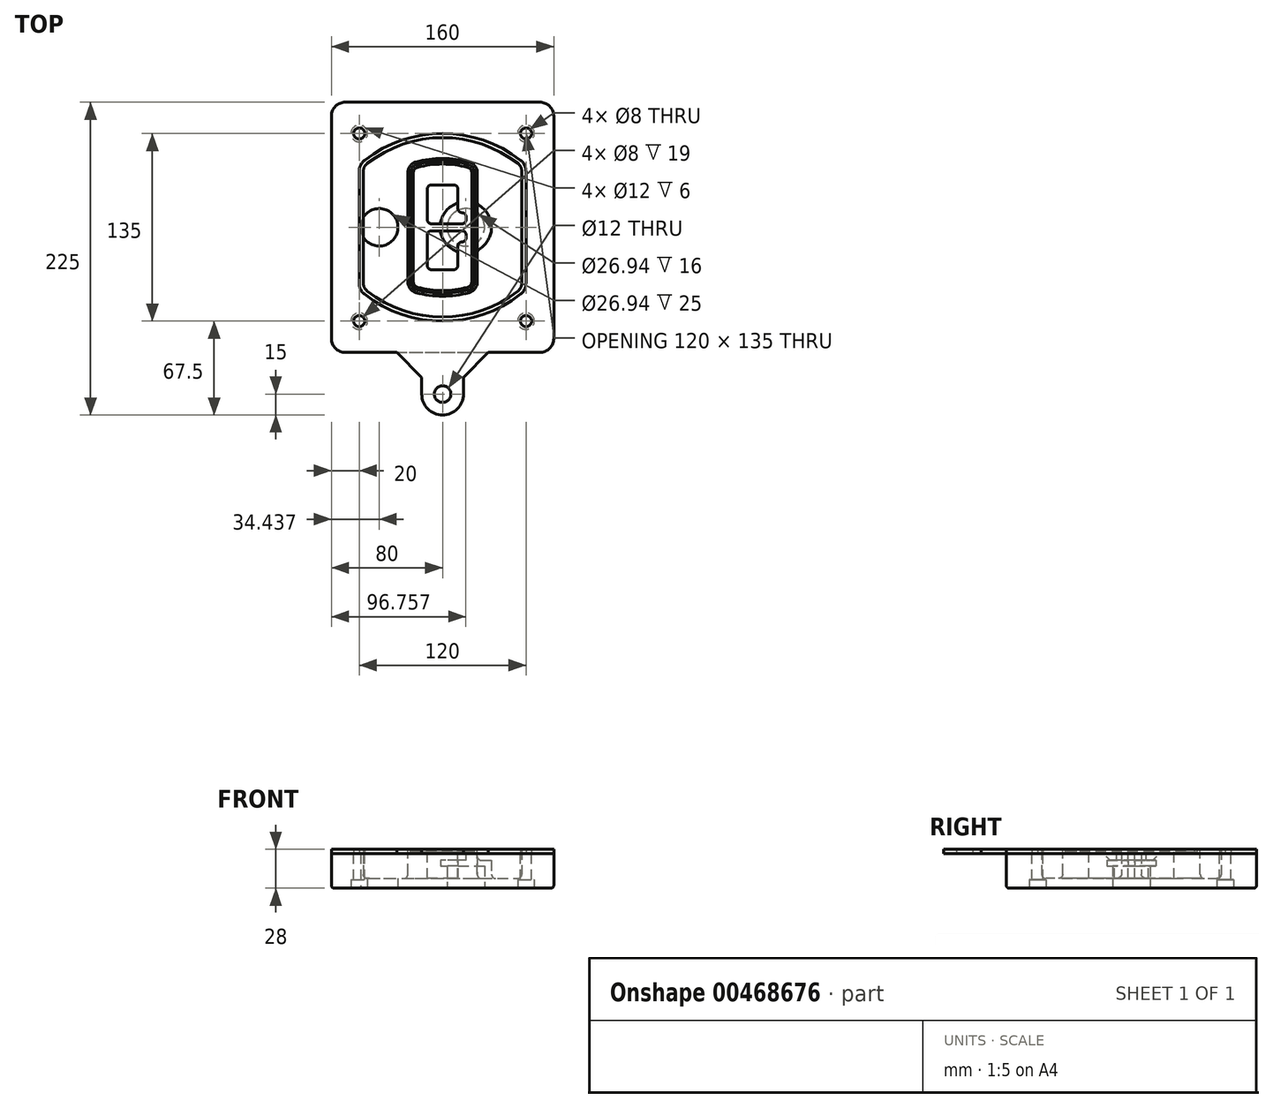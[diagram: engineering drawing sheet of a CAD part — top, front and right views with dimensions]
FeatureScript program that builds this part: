
annotation { "Feature Type Name" : "Feature", "Feature Type Description" : "" }
export const myFeature = defineFeature(function(context is Context, id is Id, definition is map)
    precondition{}
    {
        {
            var Q0;
            Q0=qCreatedBy(makeId("Top.planeOp"),FACE);
            var sketch = newSketch(context, id + "F0", { "sketchPlane" : qUnion([Q0])});
            skPoint(sketch, "E0.rect.middle", {"position": v(0, 0) * mm});
            skLineSegment(sketch, "E1.bottom", {"start": v(-70, -90) * mm, "end": v(70, -90) * mm});
            skLineSegment(sketch, "E1.top", {"start": v(-70, 90) * mm, "end": v(70, 90) * mm});
            skLineSegment(sketch, "E1.left", {"start": v(-80, -80) * mm, "end": v(-80, 80) * mm});
            skLineSegment(sketch, "E1.right", {"start": v(80, -80) * mm, "end": v(80, 80) * mm});
            skLineSegment(sketch, "E2", {"start": v(-80, 90) * mm, "end": v(80, -90) * mm, "construction": true});
            skLineSegment(sketch, "E3", {"start": v(80, 90) * mm, "end": v(-80, -90) * mm, "construction": true});
            skCircle(sketch, "E4", {"center": v(-60, 67.5) * mm, "radius": 4 * mm});
            skCircle(sketch, "E5", {"center": v(60, 67.5) * mm, "radius": 4 * mm});
            skCircle(sketch, "E6", {"center": v(60, -67.5) * mm, "radius": 4 * mm});
            skCircle(sketch, "E7", {"center": v(-60, -67.5) * mm, "radius": 4 * mm});
            skLineSegment(sketch, "E8", {"start": v(-60, 67.5) * mm, "end": v(60, 67.5) * mm, "construction": true});
            skLineSegment(sketch, "E9", {"start": v(60, 67.5) * mm, "end": v(60, -67.5) * mm, "construction": true});
            skLineSegment(sketch, "E10", {"start": v(60, -67.5) * mm, "end": v(-60, -67.5) * mm, "construction": true});
            skLineSegment(sketch, "E11", {"start": v(-60, -67.5) * mm, "end": v(-60, 67.5) * mm, "construction": true});
            skLineSegment(sketch, "E12", {"start": v(-60, 40.3) * mm, "end": v(-60, -40.3) * mm});
            skLineSegment(sketch, "E13", {"start": v(60, 40.3) * mm, "end": v(60, -40.3) * mm});
            skArc(sketch, "E14", {"start": v(56.15, 48.18) * mm, "mid": v(0, 67.5) * mm, "end": v(-56.15, 48.18) * mm});
            skArc(sketch, "E15", {"start": v(-56.15, -48.18) * mm, "mid": v(0, -67.5) * mm, "end": v(56.15, -48.18) * mm});
            skLineSegment(sketch, "E16", {"start": v(-60, 0) * mm, "end": v(60, 0) * mm, "construction": true});
            skPoint(sketch, "E17.visualSharp", {"position": v(-60, -45) * mm});
            skArc(sketch, "E17.filletArc", {"start": v(-60, -40.3) * mm, "mid": v(-58.99, -44.68) * mm, "end": v(-56.15, -48.18) * mm});
            skPoint(sketch, "E18.visualSharp", {"position": v(-60, 45) * mm});
            skArc(sketch, "E18.filletArc", {"start": v(-56.15, 48.18) * mm, "mid": v(-58.99, 44.68) * mm, "end": v(-60, 40.3) * mm});
            skPoint(sketch, "E19.visualSharp", {"position": v(60, 45) * mm});
            skArc(sketch, "E19.filletArc", {"start": v(60, 40.3) * mm, "mid": v(58.99, 44.68) * mm, "end": v(56.15, 48.18) * mm});
            skPoint(sketch, "E20.visualSharp", {"position": v(60, -45) * mm});
            skArc(sketch, "E20.filletArc", {"start": v(56.15, -48.18) * mm, "mid": v(58.99, -44.68) * mm, "end": v(60, -40.3) * mm});
            skPoint(sketch, "E21.visualSharp", {"position": v(-80, 90) * mm});
            skArc(sketch, "E21.filletArc", {"start": v(-70, 90) * mm, "mid": v(-77.07, 87.07) * mm, "end": v(-80, 80) * mm});
            skPoint(sketch, "E22.visualSharp", {"position": v(80, 90) * mm});
            skArc(sketch, "E22.filletArc", {"start": v(80, 80) * mm, "mid": v(77.07, 87.07) * mm, "end": v(70, 90) * mm});
            skPoint(sketch, "E23.visualSharp", {"position": v(80, -90) * mm});
            skArc(sketch, "E23.filletArc", {"start": v(70, -90) * mm, "mid": v(77.07, -87.07) * mm, "end": v(80, -80) * mm});
            skPoint(sketch, "E24.visualSharp", {"position": v(-80, -90) * mm});
            skArc(sketch, "E24.filletArc", {"start": v(-80, -80) * mm, "mid": v(-77.07, -87.07) * mm, "end": v(-70, -90) * mm});
            skArc(sketch, "E25.0", {"start": v(57, 40.3) * mm, "mid": v(56.3, 43.36) * mm, "end": v(54.3, 45.81) * mm});
            skLineSegment(sketch, "E25.1", {"start": v(57, 40.3) * mm, "end": v(57, -40.3) * mm});
            skArc(sketch, "E25.2", {"start": v(54.3, -45.81) * mm, "mid": v(56.3, -43.36) * mm, "end": v(57, -40.3) * mm});
            skArc(sketch, "E25.3", {"start": v(-54.3, -45.81) * mm, "mid": v(0, -64.5) * mm, "end": v(54.3, -45.81) * mm});
            skArc(sketch, "E25.4", {"start": v(-57, -40.3) * mm, "mid": v(-56.3, -43.36) * mm, "end": v(-54.3, -45.81) * mm});
            skArc(sketch, "E25.5", {"start": v(54.3, 45.81) * mm, "mid": v(0, 64.5) * mm, "end": v(-54.3, 45.81) * mm});
            skLineSegment(sketch, "E25.6", {"start": v(-57, 40.3) * mm, "end": v(-57, -40.3) * mm});
            skArc(sketch, "E25.7", {"start": v(-54.3, 45.81) * mm, "mid": v(-56.3, 43.36) * mm, "end": v(-57, 40.3) * mm});
            skArc(sketch, "E26.0", {"start": v(-58.62, 51.33) * mm, "mid": v(-62.58, 46.43) * mm, "end": v(-64, 40.3) * mm});
            skArc(sketch, "E26.1", {"start": v(58.62, 51.33) * mm, "mid": v(0, 71.5) * mm, "end": v(-58.62, 51.33) * mm});
            skArc(sketch, "E26.2", {"start": v(64, 40.3) * mm, "mid": v(62.58, 46.43) * mm, "end": v(58.62, 51.33) * mm});
            skLineSegment(sketch, "E26.3", {"start": v(64, 40.3) * mm, "end": v(64, -40.3) * mm});
            skArc(sketch, "E26.4", {"start": v(58.62, -51.33) * mm, "mid": v(62.58, -46.43) * mm, "end": v(64, -40.3) * mm});
            skLineSegment(sketch, "E26.5", {"start": v(-64, 40.3) * mm, "end": v(-64, -40.3) * mm});
            skArc(sketch, "E26.6", {"start": v(-58.62, -51.33) * mm, "mid": v(0, -71.5) * mm, "end": v(58.62, -51.33) * mm});
            skArc(sketch, "E26.7", {"start": v(-64, -40.3) * mm, "mid": v(-62.58, -46.43) * mm, "end": v(-58.62, -51.33) * mm});
            skSolve(sketch);
        }
        {
            var Q0;
            Q0=makeQuery(id+"F0.imprint","IMPRINT",FACE,{"disambiguationData":[TD([[makeQuery(id+"F0.imprint","IMPRINT",EDGE,{"derivedFrom":sQuery(id+"F0.wireOp",EDGE,"E1.bottom")}),1.0]])]});
            var Q1;
            Q1=makeQuery(id+"F0.imprint","IMPRINT",FACE,{"disambiguationData":[TD([[makeQuery(id+"F0.imprint","IMPRINT",EDGE,{"derivedFrom":sQuery(id+"F0.wireOp",EDGE,"E12")}),1.0]])]});
            var Q2;
            Q2=makeQuery(id+"F0.imprint","IMPRINT",FACE,{"disambiguationData":[TD([[makeQuery(id+"F0.imprint","IMPRINT",EDGE,{"derivedFrom":sQuery(id+"F0.wireOp",EDGE,"E25.0")}),1.0]])]});
            var Q3;
            Q3=makeQuery(id+"F0.imprint","IMPRINT",FACE,{"disambiguationData":[TD([[makeQuery(id+"F0.imprint","IMPRINT",EDGE,{"derivedFrom":sQuery(id+"F0.wireOp",EDGE,"E12")}),-1.0]])]});
            extrude(context, id + "F1", {"entities" : qUnion([Q0, Q1, Q2, Q3]), "oppositeDirection" : true, "depth" : 25 * mm});
        }
        {
            var Q0;
            Q0=makeQuery(id+"F0.imprint","IMPRINT",FACE,{"disambiguationData":[TD([[makeQuery(id+"F0.imprint","IMPRINT",EDGE,{"derivedFrom":sQuery(id+"F0.wireOp",EDGE,"E12")}),1.0]])]});
            extrude(context, id + "F2", {"entities" : qUnion([Q0]), "operationType" : NewBodyOperationType.ADD, "depth" : 3 * mm});
        }
        {
            var Q0;
            Q0=makeQuery(id+"F0.imprint","IMPRINT",FACE,{"disambiguationData":[TD([[makeQuery(id+"F0.imprint","IMPRINT",EDGE,{"derivedFrom":sQuery(id+"F0.wireOp",EDGE,"E25.0")}),1.0]])]});
            extrude(context, id + "F3", {"entities" : qUnion([Q0]), "operationType" : NewBodyOperationType.REMOVE, "oppositeDirection" : true, "depth" : 18 * mm});
        }
        {
            var Q0;
            Q0=makeQuery(id+"F2.opExtrude","CAP_FACE",FACE,{"disambiguationData":[OSD([sQuery(id+"F0.wireOp",EDGE,"E12"),sQuery(id+"F0.wireOp",EDGE,"E13"),sQuery(id+"F0.wireOp",EDGE,"E14"),sQuery(id+"F0.wireOp",EDGE,"E15"),sQuery(id+"F0.wireOp",EDGE,"E17.filletArc"),sQuery(id+"F0.wireOp",EDGE,"E18.filletArc"),sQuery(id+"F0.wireOp",EDGE,"E19.filletArc"),sQuery(id+"F0.wireOp",EDGE,"E20.filletArc"),sQuery(id+"F0.wireOp",EDGE,"E25.0"),sQuery(id+"F0.wireOp",EDGE,"E25.1"),sQuery(id+"F0.wireOp",EDGE,"E25.2"),sQuery(id+"F0.wireOp",EDGE,"E25.3"),sQuery(id+"F0.wireOp",EDGE,"E25.4"),sQuery(id+"F0.wireOp",EDGE,"E25.5"),sQuery(id+"F0.wireOp",EDGE,"E25.6"),sQuery(id+"F0.wireOp",EDGE,"E25.7")])],"isStart":false});
            var sketch = newSketch(context, id + "F4", { "sketchPlane" : qUnion([Q0])});
            skArc(sketch, "E27.0", {"start": v(-19.08, -46.97) * mm, "mid": v(0, -49.5) * mm, "end": v(19.08, -46.97) * mm});
            skArc(sketch, "E28.0", {"start": v(19.08, 46.97) * mm, "mid": v(0, 49.5) * mm, "end": v(-19.08, 46.97) * mm});
            skLineSegment(sketch, "E29", {"start": v(-25, 39.25) * mm, "end": v(-25, -39.25) * mm});
            skLineSegment(sketch, "E30", {"start": v(25, 39.25) * mm, "end": v(25, -39.25) * mm});
            skLineSegment(sketch, "E31", {"start": v(-25, 45.1) * mm, "end": v(25, 45.1) * mm, "construction": true});
            skLineSegment(sketch, "E32", {"start": v(-25, -45.1) * mm, "end": v(25, -45.1) * mm, "construction": true});
            skPoint(sketch, "E33.visualSharp", {"position": v(-25, 45.1) * mm});
            skArc(sketch, "E33.filletArc", {"start": v(-19.08, 46.97) * mm, "mid": v(-23.35, 44.11) * mm, "end": v(-25, 39.25) * mm});
            skPoint(sketch, "E34.visualSharp", {"position": v(25, 45.1) * mm});
            skArc(sketch, "E34.filletArc", {"start": v(25, 39.25) * mm, "mid": v(23.35, 44.11) * mm, "end": v(19.08, 46.97) * mm});
            skPoint(sketch, "E35.visualSharp", {"position": v(25, -45.1) * mm});
            skArc(sketch, "E35.filletArc", {"start": v(19.08, -46.97) * mm, "mid": v(23.35, -44.11) * mm, "end": v(25, -39.25) * mm});
            skPoint(sketch, "E36.visualSharp", {"position": v(-25, -45.1) * mm});
            skArc(sketch, "E36.filletArc", {"start": v(-25, -39.25) * mm, "mid": v(-23.35, -44.11) * mm, "end": v(-19.08, -46.97) * mm});
            skArc(sketch, "E37.0", {"start": v(54.3, 45.81) * mm, "mid": v(0, 64.5) * mm, "end": v(-54.3, 45.81) * mm});
            skArc(sketch, "E37.1", {"start": v(-54.3, 45.81) * mm, "mid": v(-56.3, 43.36) * mm, "end": v(-57, 40.3) * mm});
            skLineSegment(sketch, "E37.2", {"start": v(-57, 40.3) * mm, "end": v(-57, -40.3) * mm});
            skArc(sketch, "E37.3", {"start": v(-57, -40.3) * mm, "mid": v(-56.3, -43.36) * mm, "end": v(-54.3, -45.81) * mm});
            skArc(sketch, "E37.4", {"start": v(-54.3, -45.81) * mm, "mid": v(0, -64.5) * mm, "end": v(54.3, -45.81) * mm});
            skArc(sketch, "E37.5", {"start": v(54.3, -45.81) * mm, "mid": v(56.3, -43.36) * mm, "end": v(57, -40.3) * mm});
            skLineSegment(sketch, "E37.6", {"start": v(57, 40.3) * mm, "end": v(57, -40.3) * mm});
            skArc(sketch, "E37.7", {"start": v(57, 40.3) * mm, "mid": v(56.3, 43.36) * mm, "end": v(54.3, 45.81) * mm});
            skLineSegment(sketch, "E38.0", {"start": v(23, 39.25) * mm, "end": v(23, -39.25) * mm});
            skArc(sketch, "E38.1", {"start": v(18.56, -45.04) * mm, "mid": v(21.76, -42.9) * mm, "end": v(23, -39.25) * mm});
            skArc(sketch, "E38.2", {"start": v(-18.56, -45.04) * mm, "mid": v(0, -47.5) * mm, "end": v(18.56, -45.04) * mm});
            skArc(sketch, "E38.3", {"start": v(-23, -39.25) * mm, "mid": v(-21.76, -42.9) * mm, "end": v(-18.56, -45.04) * mm});
            skLineSegment(sketch, "E38.4", {"start": v(-23, 39.25) * mm, "end": v(-23, -39.25) * mm});
            skArc(sketch, "E38.5", {"start": v(23, 39.25) * mm, "mid": v(21.76, 42.9) * mm, "end": v(18.56, 45.04) * mm});
            skArc(sketch, "E38.6", {"start": v(-18.56, 45.04) * mm, "mid": v(-21.76, 42.9) * mm, "end": v(-23, 39.25) * mm});
            skArc(sketch, "E38.7", {"start": v(18.56, 45.04) * mm, "mid": v(0, 47.5) * mm, "end": v(-18.56, 45.04) * mm});
            skArc(sketch, "E39.0", {"start": v(21, 39.25) * mm, "mid": v(20.18, 41.68) * mm, "end": v(18.04, 43.1) * mm});
            skLineSegment(sketch, "E39.1", {"start": v(21, 39.25) * mm, "end": v(21, -39.25) * mm});
            skArc(sketch, "E39.2", {"start": v(18.04, -43.1) * mm, "mid": v(20.18, -41.68) * mm, "end": v(21, -39.25) * mm});
            skArc(sketch, "E39.3", {"start": v(-18.04, -43.1) * mm, "mid": v(0, -45.5) * mm, "end": v(18.04, -43.1) * mm});
            skArc(sketch, "E39.4", {"start": v(-21, -39.25) * mm, "mid": v(-20.18, -41.68) * mm, "end": v(-18.04, -43.1) * mm});
            skArc(sketch, "E39.5", {"start": v(18.04, 43.1) * mm, "mid": v(0, 45.5) * mm, "end": v(-18.04, 43.1) * mm});
            skLineSegment(sketch, "E39.6", {"start": v(-21, 39.25) * mm, "end": v(-21, -39.25) * mm});
            skArc(sketch, "E39.7", {"start": v(-18.04, 43.1) * mm, "mid": v(-20.18, 41.68) * mm, "end": v(-21, 39.25) * mm});
            skLineSegment(sketch, "E40", {"start": v(-25, 0) * mm, "end": v(25, 0) * mm, "construction": true});
            skLineSegment(sketch, "E41", {"start": v(-11, 5.5) * mm, "end": v(-11, 27.5) * mm});
            skLineSegment(sketch, "E42", {"start": v(-8, 30.5) * mm, "end": v(8, 30.5) * mm});
            skLineSegment(sketch, "E43", {"start": v(11, 27.5) * mm, "end": v(11, 13.5) * mm});
            skLineSegment(sketch, "E44", {"start": v(14, 10.5) * mm, "end": v(14, 10.5) * mm});
            skLineSegment(sketch, "E45", {"start": v(17, 7.5) * mm, "end": v(17, 5.5) * mm});
            skLineSegment(sketch, "E46", {"start": v(14, 2.5) * mm, "end": v(-8, 2.5) * mm});
            skPoint(sketch, "E47.visualSharp", {"position": v(-11, 30.5) * mm});
            skArc(sketch, "E47.filletArc", {"start": v(-8, 30.5) * mm, "mid": v(-10.12, 29.62) * mm, "end": v(-11, 27.5) * mm});
            skPoint(sketch, "E48.visualSharp", {"position": v(11, 30.5) * mm});
            skArc(sketch, "E48.filletArc", {"start": v(11, 27.5) * mm, "mid": v(10.12, 29.62) * mm, "end": v(8, 30.5) * mm});
            skPoint(sketch, "E49.visualSharp", {"position": v(11, 10.5) * mm});
            skArc(sketch, "E49.filletArc", {"start": v(11, 13.5) * mm, "mid": v(11.88, 11.38) * mm, "end": v(14, 10.5) * mm});
            skPoint(sketch, "E50.visualSharp", {"position": v(17, 10.5) * mm});
            skArc(sketch, "E50.filletArc", {"start": v(17, 7.5) * mm, "mid": v(16.12, 9.62) * mm, "end": v(14, 10.5) * mm});
            skPoint(sketch, "E51.visualSharp", {"position": v(17, 2.5) * mm});
            skArc(sketch, "E51.filletArc", {"start": v(14, 2.5) * mm, "mid": v(16.12, 3.38) * mm, "end": v(17, 5.5) * mm});
            skPoint(sketch, "E52.visualSharp", {"position": v(-11, 2.5) * mm});
            skArc(sketch, "E52.filletArc", {"start": v(-11, 5.5) * mm, "mid": v(-10.12, 3.38) * mm, "end": v(-8, 2.5) * mm});
            skLineSegment(sketch, "E53.0.MirrorCS", {"start": v(14, -2.5) * mm, "end": v(-8, -2.5) * mm});
            skArc(sketch, "E54.0.MirrorCS", {"start": v(-11, -5.5) * mm, "mid": v(-10.12, -3.38) * mm, "end": v(-8, -2.5) * mm});
            skLineSegment(sketch, "E55.0.MirrorCS", {"start": v(-11, -5.5) * mm, "end": v(-11, -27.5) * mm});
            skArc(sketch, "E56.0.MirrorCS", {"start": v(-8, -30.5) * mm, "mid": v(-10.12, -29.62) * mm, "end": v(-11, -27.5) * mm});
            skLineSegment(sketch, "E57.0.MirrorCS", {"start": v(-8, -30.5) * mm, "end": v(8, -30.5) * mm});
            skArc(sketch, "E58.0.MirrorCS", {"start": v(11, -27.5) * mm, "mid": v(10.12, -29.62) * mm, "end": v(8, -30.5) * mm});
            skLineSegment(sketch, "E59.0.MirrorCS", {"start": v(11, -27.5) * mm, "end": v(11, -13.5) * mm});
            skArc(sketch, "E60.0.MirrorCS", {"start": v(11, -13.5) * mm, "mid": v(11.88, -11.38) * mm, "end": v(14, -10.5) * mm});
            skArc(sketch, "E61.0.MirrorCS", {"start": v(17, -7.5) * mm, "mid": v(16.12, -9.62) * mm, "end": v(14, -10.5) * mm});
            skLineSegment(sketch, "E62.0.MirrorCS", {"start": v(17, -7.5) * mm, "end": v(17, -5.5) * mm});
            skArc(sketch, "E63.0.MirrorCS", {"start": v(14, -2.5) * mm, "mid": v(16.12, -3.38) * mm, "end": v(17, -5.5) * mm});
            skSolve(sketch);
        }
        {
            var Q0;
            Q0=makeQuery(id+"F4.imprint","IMPRINT",FACE,{"disambiguationData":[TD([[makeQuery(id+"F4.imprint","IMPRINT",EDGE,{"derivedFrom":sQuery(id+"F4.wireOp",EDGE,"E27.0")}),1.0]])]});
            var Q1;
            Q1=makeQuery(id+"F4.imprint","IMPRINT",FACE,{"disambiguationData":[TD([[makeQuery(id+"F4.imprint","IMPRINT",EDGE,{"derivedFrom":sQuery(id+"F4.wireOp",EDGE,"E38.0")}),-1.0]])]});
            var Q2;
            Q2=makeQuery(id+"F4.imprint","IMPRINT",FACE,{"disambiguationData":[TD([[makeQuery(id+"F4.imprint","IMPRINT",EDGE,{"derivedFrom":sQuery(id+"F4.wireOp",EDGE,"E39.0")}),1.0]])]});
            extrude(context, id + "F5", {"entities" : qUnion([Q0, Q1, Q2]), "operationType" : NewBodyOperationType.ADD, "endBound" : BoundingType.UP_TO_NEXT, "oppositeDirection" : true, "depth" : 25 * mm});
        }
        {
            var Q0;
            Q0=makeQuery(id+"F4.imprint","IMPRINT",FACE,{"disambiguationData":[TD([[makeQuery(id+"F4.imprint","IMPRINT",EDGE,{"derivedFrom":sQuery(id+"F4.wireOp",EDGE,"E38.0")}),-1.0]])]});
            extrude(context, id + "F6", {"entities" : qUnion([Q0]), "operationType" : NewBodyOperationType.REMOVE, "oppositeDirection" : true, "depth" : 2 * mm});
        }
        {
            var Q0;
            Q0=makeQuery(id+"F1.opExtrude","CAP_FACE",FACE,{"disambiguationData":[OSD([sQuery(id+"F0.wireOp",EDGE,"E1.bottom"),sQuery(id+"F0.wireOp",EDGE,"E1.top"),sQuery(id+"F0.wireOp",EDGE,"E1.left"),sQuery(id+"F0.wireOp",EDGE,"E1.right"),sQuery(id+"F0.wireOp",EDGE,"E4"),sQuery(id+"F0.wireOp",EDGE,"E5"),sQuery(id+"F0.wireOp",EDGE,"E6"),sQuery(id+"F0.wireOp",EDGE,"E7"),sQuery(id+"F0.wireOp",EDGE,"E21.filletArc"),sQuery(id+"F0.wireOp",EDGE,"E22.filletArc"),sQuery(id+"F0.wireOp",EDGE,"E23.filletArc"),sQuery(id+"F0.wireOp",EDGE,"E24.filletArc")])],"isStart":false});
            var sketch = newSketch(context, id + "F7", { "sketchPlane" : qUnion([Q0])});
            skCircle(sketch, "E64", {"center": v(16.76, 0) * mm, "radius": 13.47 * mm});
            skCircle(sketch, "E65", {"center": v(-45.56, 0) * mm, "radius": 13.47 * mm});
            skLineSegment(sketch, "E66", {"start": v(80, 0) * mm, "end": v(-80, 0) * mm});
            skCircle(sketch, "E67", {"center": v(16.76, 0) * mm, "radius": 18.47 * mm});
            skCircle(sketch, "E68", {"center": v(60, -67.5) * mm, "radius": 6 * mm});
            skCircle(sketch, "E69", {"center": v(-60, -67.5) * mm, "radius": 6 * mm});
            skCircle(sketch, "E70", {"center": v(-60, 67.5) * mm, "radius": 6 * mm});
            skCircle(sketch, "E71", {"center": v(60, 67.5) * mm, "radius": 6 * mm});
            skSolve(sketch);
        }
        {
            var Q0;
            {var subQ1=sQuery(id+"F7.wireOp",EDGE,"E66");var subQ4=sQuery(id+"F7.wireOp",EDGE,"E64");var subQ6=makeQuery(id+"F7.imprint","INTERSECT",VERTEX,{"disambiguationData":[OD(0.0)],"derivedFrom":[subQ4,subQ1]});Q0=makeQuery(id+"F7.imprint","IMPRINT",FACE,{"disambiguationData":[TD([[makeQuery(id+"F7.imprint","IMPRINT",EDGE,{"disambiguationData":[TD([[subQ6,-1.0]])],"derivedFrom":subQ4}),-1.0]])]});}
            var Q1;
            {var subQ0=sQuery(id+"F7.wireOp",EDGE,"E66");var subQ1=sQuery(id+"F7.wireOp",EDGE,"E64");var subQ3=makeQuery(id+"F7.imprint","INTERSECT",VERTEX,{"disambiguationData":[OD(0.0)],"derivedFrom":[subQ1,subQ0]});Q1=makeQuery(id+"F7.imprint","IMPRINT",FACE,{"disambiguationData":[TD([[makeQuery(id+"F7.imprint","IMPRINT",EDGE,{"disambiguationData":[TD([[subQ3,-1.0]])],"derivedFrom":subQ1}),1.0]])]});}
            var Q2;
            {var subQ0=sQuery(id+"F7.wireOp",EDGE,"E66");var subQ1=sQuery(id+"F7.wireOp",EDGE,"E64");var subQ3=makeQuery(id+"F7.imprint","INTERSECT",VERTEX,{"disambiguationData":[OD(0.0)],"derivedFrom":[subQ1,subQ0]});Q2=makeQuery(id+"F7.imprint","IMPRINT",FACE,{"disambiguationData":[TD([[makeQuery(id+"F7.imprint","IMPRINT",EDGE,{"disambiguationData":[TD([[subQ3,1.0]])],"derivedFrom":subQ1}),1.0]])]});}
            var Q3;
            {var subQ1=sQuery(id+"F7.wireOp",EDGE,"E66");var subQ4=sQuery(id+"F7.wireOp",EDGE,"E64");var subQ6=makeQuery(id+"F7.imprint","INTERSECT",VERTEX,{"disambiguationData":[OD(0.0)],"derivedFrom":[subQ4,subQ1]});Q3=makeQuery(id+"F7.imprint","IMPRINT",FACE,{"disambiguationData":[TD([[makeQuery(id+"F7.imprint","IMPRINT",EDGE,{"disambiguationData":[TD([[subQ6,1.0]])],"derivedFrom":subQ4}),-1.0]])]});}
            extrude(context, id + "F8", {"entities" : qUnion([Q0, Q1, Q2, Q3]), "operationType" : NewBodyOperationType.ADD, "oppositeDirection" : true, "depth" : 20 * mm});
        }
        {
            var Q0;
            {var subQ0=sQuery(id+"F7.wireOp",EDGE,"E66");var subQ1=sQuery(id+"F7.wireOp",EDGE,"E64");var subQ3=makeQuery(id+"F7.imprint","INTERSECT",VERTEX,{"disambiguationData":[OD(0.0)],"derivedFrom":[subQ1,subQ0]});Q0=makeQuery(id+"F7.imprint","IMPRINT",FACE,{"disambiguationData":[TD([[makeQuery(id+"F7.imprint","IMPRINT",EDGE,{"disambiguationData":[TD([[subQ3,-1.0]])],"derivedFrom":subQ1}),1.0]])]});}
            var Q1;
            {var subQ0=sQuery(id+"F7.wireOp",EDGE,"E66");var subQ1=sQuery(id+"F7.wireOp",EDGE,"E64");var subQ3=makeQuery(id+"F7.imprint","INTERSECT",VERTEX,{"disambiguationData":[OD(0.0)],"derivedFrom":[subQ1,subQ0]});Q1=makeQuery(id+"F7.imprint","IMPRINT",FACE,{"disambiguationData":[TD([[makeQuery(id+"F7.imprint","IMPRINT",EDGE,{"disambiguationData":[TD([[subQ3,1.0]])],"derivedFrom":subQ1}),1.0]])]});}
            extrude(context, id + "F9", {"entities" : qUnion([Q0, Q1]), "operationType" : NewBodyOperationType.REMOVE, "oppositeDirection" : true, "depth" : 16 * mm});
        }
        {
            var Q0;
            {var subQ0=sQuery(id+"F7.wireOp",EDGE,"E66");var subQ1=sQuery(id+"F7.wireOp",EDGE,"E65");var subQ3=makeQuery(id+"F7.imprint","INTERSECT",VERTEX,{"disambiguationData":[OD(0.0)],"derivedFrom":[subQ1,subQ0]});Q0=makeQuery(id+"F7.imprint","IMPRINT",FACE,{"disambiguationData":[TD([[makeQuery(id+"F7.imprint","IMPRINT",EDGE,{"disambiguationData":[TD([[subQ3,-1.0]])],"derivedFrom":subQ1}),1.0]])]});}
            var Q1;
            {var subQ0=sQuery(id+"F7.wireOp",EDGE,"E66");var subQ1=sQuery(id+"F7.wireOp",EDGE,"E65");var subQ3=makeQuery(id+"F7.imprint","INTERSECT",VERTEX,{"disambiguationData":[OD(0.0)],"derivedFrom":[subQ1,subQ0]});Q1=makeQuery(id+"F7.imprint","IMPRINT",FACE,{"disambiguationData":[TD([[makeQuery(id+"F7.imprint","IMPRINT",EDGE,{"disambiguationData":[TD([[subQ3,1.0]])],"derivedFrom":subQ1}),1.0]])]});}
            extrude(context, id + "F10", {"entities" : qUnion([Q0, Q1]), "operationType" : NewBodyOperationType.REMOVE, "oppositeDirection" : true, "depth" : 25 * mm});
        }
        {
            var Q0;
            Q0=makeQuery(id+"F7.imprint","IMPRINT",FACE,{"disambiguationData":[TD([[makeQuery(id+"F7.imprint","IMPRINT",EDGE,{"derivedFrom":sQuery(id+"F7.wireOp",EDGE,"E68")}),1.0]])]});
            var Q1;
            Q1=makeQuery(id+"F7.imprint","IMPRINT",FACE,{"disambiguationData":[TD([[makeQuery(id+"F7.imprint","IMPRINT",EDGE,{"derivedFrom":makeQuery(id+"F1.opExtrude","CAP_EDGE",EDGE,{"disambiguationData":[OSD([sQuery(id+"F0.wireOp",EDGE,"E5")])],"isStart":false})}),-1.0]])]});
            var Q2;
            Q2=makeQuery(id+"F7.imprint","IMPRINT",FACE,{"disambiguationData":[TD([[makeQuery(id+"F7.imprint","IMPRINT",EDGE,{"derivedFrom":sQuery(id+"F7.wireOp",EDGE,"E69")}),1.0]])]});
            var Q3;
            Q3=makeQuery(id+"F7.imprint","IMPRINT",FACE,{"disambiguationData":[TD([[makeQuery(id+"F7.imprint","IMPRINT",EDGE,{"derivedFrom":makeQuery(id+"F1.opExtrude","CAP_EDGE",EDGE,{"disambiguationData":[OSD([sQuery(id+"F0.wireOp",EDGE,"E4")])],"isStart":false})}),-1.0]])]});
            var Q4;
            Q4=makeQuery(id+"F7.imprint","IMPRINT",FACE,{"disambiguationData":[TD([[makeQuery(id+"F7.imprint","IMPRINT",EDGE,{"derivedFrom":sQuery(id+"F7.wireOp",EDGE,"E70")}),1.0]])]});
            var Q5;
            Q5=makeQuery(id+"F7.imprint","IMPRINT",FACE,{"disambiguationData":[TD([[makeQuery(id+"F7.imprint","IMPRINT",EDGE,{"derivedFrom":makeQuery(id+"F1.opExtrude","CAP_EDGE",EDGE,{"disambiguationData":[OSD([sQuery(id+"F0.wireOp",EDGE,"E7")])],"isStart":false})}),-1.0]])]});
            var Q6;
            Q6=makeQuery(id+"F7.imprint","IMPRINT",FACE,{"disambiguationData":[TD([[makeQuery(id+"F7.imprint","IMPRINT",EDGE,{"derivedFrom":sQuery(id+"F7.wireOp",EDGE,"E71")}),1.0]])]});
            var Q7;
            Q7=makeQuery(id+"F7.imprint","IMPRINT",FACE,{"disambiguationData":[TD([[makeQuery(id+"F7.imprint","IMPRINT",EDGE,{"derivedFrom":makeQuery(id+"F1.opExtrude","CAP_EDGE",EDGE,{"disambiguationData":[OSD([sQuery(id+"F0.wireOp",EDGE,"E6")])],"isStart":false})}),-1.0]])]});
            extrude(context, id + "F11", {"entities" : qUnion([Q0, Q1, Q2, Q3, Q4, Q5, Q6, Q7]), "operationType" : NewBodyOperationType.REMOVE, "oppositeDirection" : true, "depth" : 6 * mm});
        }
        {
            var Q0;
            Q0=makeQuery(id+"F9.boolean.opBoolean","COPY",FACE,{"derivedFrom":makeQuery(id+"F9.opExtrude","CAP_FACE",FACE,{"disambiguationData":[OSD([sQuery(id+"F7.wireOp",EDGE,"E64")])],"isStart":false})});
            var sketch = newSketch(context, id + "F12", { "sketchPlane" : qUnion([Q0])});
            skArc(sketch, "E72.0", {"start": v(11, 17.55) * mm, "mid": v(2.57, 11.82) * mm, "end": v(-1.54, 2.5) * mm});
            skArc(sketch, "E72.1", {"start": v(-1.54, -2.5) * mm, "mid": v(2.57, -11.82) * mm, "end": v(11, -17.55) * mm});
            skLineSegment(sketch, "E73", {"start": v(-1.54, -2.5) * mm, "end": v(14, -2.5) * mm});
            skLineSegment(sketch, "E74.0", {"start": v(14, 2.5) * mm, "end": v(-1.54, 2.5) * mm});
            skArc(sketch, "E74.1", {"start": v(14, 2.5) * mm, "mid": v(16.12, 3.38) * mm, "end": v(17, 5.5) * mm});
            skLineSegment(sketch, "E74.2", {"start": v(17, 7.5) * mm, "end": v(17, 5.5) * mm});
            skArc(sketch, "E74.3", {"start": v(17, 7.5) * mm, "mid": v(16.12, 9.62) * mm, "end": v(14, 10.5) * mm});
            skArc(sketch, "E74.4", {"start": v(11, 13.5) * mm, "mid": v(11.88, 11.38) * mm, "end": v(14, 10.5) * mm});
            skLineSegment(sketch, "E74.5", {"start": v(11, 17.55) * mm, "end": v(11, 13.5) * mm});
            skLineSegment(sketch, "E74.7", {"start": v(14, -2.5) * mm, "end": v(-1.54, -2.5) * mm});
            skArc(sketch, "E74.8", {"start": v(14, -2.5) * mm, "mid": v(16.12, -3.38) * mm, "end": v(17, -5.5) * mm});
            skLineSegment(sketch, "E74.9", {"start": v(17, -7.5) * mm, "end": v(17, -5.5) * mm});
            skArc(sketch, "E74.10", {"start": v(17, -7.5) * mm, "mid": v(16.12, -9.62) * mm, "end": v(14, -10.5) * mm});
            skArc(sketch, "E74.11", {"start": v(11, -13.5) * mm, "mid": v(11.88, -11.38) * mm, "end": v(14, -10.5) * mm});
            skLineSegment(sketch, "E74.12", {"start": v(11, -17.55) * mm, "end": v(11, -13.5) * mm});
            skPoint(sketch, "E75.orphan", {"position": v(11, -27.5) * mm});
            skPoint(sketch, "E76.orphan", {"position": v(-8, -2.5) * mm});
            skPoint(sketch, "E77.orphan", {"position": v(-8, 2.5) * mm});
            skPoint(sketch, "E78.orphan", {"position": v(11, 27.5) * mm});
            skSolve(sketch);
        }
        {
            var Q0;
            {var subQ7=sQuery(id+"F12.wireOp",EDGE,"E72.0");var subQ14=sQuery(id+"F12.wireOp",EDGE,"E72.1");var subQ16=sQuery(id+"F12.wireOp",EDGE,"E74.1");var subQ18=sQuery(id+"F12.wireOp",EDGE,"E74.8");Q0=qUnion([makeQuery(id+"F12.imprint","IMPRINT",FACE,{"disambiguationData":[TD([[makeQuery(id+"F12.imprint","IMPRINT",EDGE,{"derivedFrom":subQ7}),1.0]])]}),makeQuery(id+"F12.imprint","IMPRINT",FACE,{"disambiguationData":[TD([[makeQuery(id+"F12.imprint","IMPRINT",EDGE,{"derivedFrom":subQ14}),1.0]])]}),makeQuery(id+"F12.imprint","IMPRINT",FACE,{"disambiguationData":[TD([[makeQuery(id+"F12.imprint","IMPRINT",EDGE,{"derivedFrom":subQ16}),1.0]])]}),makeQuery(id+"F12.imprint","IMPRINT",FACE,{"disambiguationData":[TD([[makeQuery(id+"F12.imprint","IMPRINT",EDGE,{"derivedFrom":subQ18}),-1.0]])]})]);}
            var Q1;
            Q1=makeQuery(id+"F5.boolean.opBoolean","SPLIT",FACE,{"disambiguationData":[TD([makeQuery(id+"F5.opExtrude","SWEPT_FACE",FACE,{"disambiguationData":[OSD([sQuery(id+"F4.wireOp",EDGE,"E41")])]})])],"derivedFrom":makeQuery(id+"F3.boolean.opBoolean","COPY",FACE,{"derivedFrom":makeQuery(id+"F3.opExtrude","CAP_FACE",FACE,{"disambiguationData":[OSD([sQuery(id+"F0.wireOp",EDGE,"E25.0"),sQuery(id+"F0.wireOp",EDGE,"E25.1"),sQuery(id+"F0.wireOp",EDGE,"E25.2"),sQuery(id+"F0.wireOp",EDGE,"E25.3"),sQuery(id+"F0.wireOp",EDGE,"E25.4"),sQuery(id+"F0.wireOp",EDGE,"E25.5"),sQuery(id+"F0.wireOp",EDGE,"E25.6"),sQuery(id+"F0.wireOp",EDGE,"E25.7")])],"isStart":false})})});
            extrude(context, id + "F13", {"entities" : qUnion([Q0]), "operationType" : NewBodyOperationType.REMOVE, "endBound" : BoundingType.UP_TO_SURFACE, "endBoundEntityFace" : qUnion([Q1]), "depth" : 25 * mm});
        }
        {
            var Q0;
            Q0=makeQuery(id+"F3.boolean.opBoolean","COPY",EDGE,{"derivedFrom":makeQuery(id+"F3.opExtrude","CAP_EDGE",EDGE,{"disambiguationData":[OSD([sQuery(id+"F0.wireOp",EDGE,"E25.6")])],"isStart":false})});
            var Q1;
            Q1=makeQuery(id+"F8.boolean.opBoolean","INTERSECT",EDGE,{"derivedFrom":[makeQuery(id+"F5.opExtrude","SWEPT_FACE",FACE,{"disambiguationData":[OSD([sQuery(id+"F4.wireOp",EDGE,"E30")])]}),makeQuery(id+"F8.opExtrude","CAP_FACE",FACE,{"disambiguationData":[OSD([sQuery(id+"F7.wireOp",EDGE,"E67")])],"isStart":false})]});
            var Q2;
            Q2=makeQuery(id+"F8.boolean.opBoolean","INTERSECT",EDGE,{"disambiguationData":[OD(1.0)],"derivedFrom":[makeQuery(id+"F5.opExtrude","SWEPT_FACE",FACE,{"disambiguationData":[OSD([sQuery(id+"F4.wireOp",EDGE,"E30")])]}),makeQuery(id+"F8.opExtrude","SWEPT_FACE",FACE,{"disambiguationData":[OSD([sQuery(id+"F7.wireOp",EDGE,"E67")])]})]});
            var Q3;
            {var subQ0=sQuery(id+"F4.wireOp",EDGE,"E30");Q3=makeQuery(id+"F8.boolean.opBoolean","SPLIT",EDGE,{"disambiguationData":[TD([makeQuery(id+"F5.opExtrude","SWEPT_FACE",FACE,{"disambiguationData":[OSD([sQuery(id+"F4.wireOp",EDGE,"E35.filletArc")])]})])],"derivedFrom":makeQuery(id+"F5.opExtrude","CAP_EDGE",EDGE,{"disambiguationData":[OSD([subQ0])],"isStart":false})});}
            var Q4;
            {var subQ0=sQuery(id+"F0.wireOp",EDGE,"E25.7");var subQ1=sQuery(id+"F0.wireOp",EDGE,"E25.1");var subQ2=sQuery(id+"F0.wireOp",EDGE,"E25.6");var subQ3=sQuery(id+"F0.wireOp",EDGE,"E25.5");var subQ4=sQuery(id+"F0.wireOp",EDGE,"E25.4");var subQ5=sQuery(id+"F0.wireOp",EDGE,"E25.0");var subQ6=sQuery(id+"F0.wireOp",EDGE,"E25.2");var subQ7=sQuery(id+"F0.wireOp",EDGE,"E25.3");Q4=makeQuery(id+"F8.boolean.opBoolean","INTERSECT",EDGE,{"derivedFrom":[makeQuery(id+"F5.boolean.opBoolean","SPLIT",FACE,{"disambiguationData":[TD([makeQuery(id+"F2.opExtrude","SWEPT_FACE",FACE,{"disambiguationData":[OSD([subQ5])]})])],"derivedFrom":makeQuery(id+"F3.boolean.opBoolean","COPY",FACE,{"derivedFrom":makeQuery(id+"F3.opExtrude","CAP_FACE",FACE,{"disambiguationData":[OSD([subQ5,subQ1,subQ6,subQ7,subQ4,subQ3,subQ2,subQ0])],"isStart":false})})}),makeQuery(id+"F8.opExtrude","SWEPT_FACE",FACE,{"disambiguationData":[OSD([sQuery(id+"F7.wireOp",EDGE,"E67")])]})]});}
            var Q5;
            Q5=makeQuery(id+"F8.boolean.opBoolean","INTERSECT",EDGE,{"disambiguationData":[OD(0.0)],"derivedFrom":[makeQuery(id+"F5.opExtrude","SWEPT_FACE",FACE,{"disambiguationData":[OSD([sQuery(id+"F4.wireOp",EDGE,"E30")])]}),makeQuery(id+"F8.opExtrude","SWEPT_FACE",FACE,{"disambiguationData":[OSD([sQuery(id+"F7.wireOp",EDGE,"E67")])]})]});
            fillet(context, id + "F14", {"entities" : qUnion([Q0, Q1, Q2, Q3, Q4, Q5]), "radius" : 3 * mm, "tangentPropagation" : true, "allowEdgeOverflow" : false});
        }
        {
            var Q0;
            Q0=makeQuery(id+"F1.opExtrude","CAP_EDGE",EDGE,{"disambiguationData":[OSD([sQuery(id+"F0.wireOp",EDGE,"E1.bottom")])],"isStart":false});
            fillet(context, id + "F15", {"entities" : qUnion([Q0]), "radius" : 2 * mm, "tangentPropagation" : true, "allowEdgeOverflow" : false});
        }
        {
            var Q0;
            {var subQ0=sQuery(id+"F0.wireOp",EDGE,"E21.filletArc");var subQ1=sQuery(id+"F0.wireOp",EDGE,"E7");var subQ2=sQuery(id+"F0.wireOp",EDGE,"E6");var subQ3=sQuery(id+"F0.wireOp",EDGE,"E5");var subQ4=sQuery(id+"F0.wireOp",EDGE,"E4");var subQ5=sQuery(id+"F0.wireOp",EDGE,"E22.filletArc");var subQ6=sQuery(id+"F0.wireOp",EDGE,"E1.bottom");var subQ7=sQuery(id+"F0.wireOp",EDGE,"E1.right");var subQ8=sQuery(id+"F0.wireOp",EDGE,"E1.top");var subQ9=sQuery(id+"F0.wireOp",EDGE,"E1.left");var subQ10=sQuery(id+"F0.wireOp",EDGE,"E23.filletArc");var subQ11=sQuery(id+"F0.wireOp",EDGE,"E24.filletArc");Q0=makeQuery(id+"F2.boolean.opBoolean","SPLIT",FACE,{"disambiguationData":[TD([makeQuery(id+"F1.opExtrude","SWEPT_FACE",FACE,{"disambiguationData":[OSD([subQ6])]})])],"derivedFrom":makeQuery(id+"F1.opExtrude","CAP_FACE",FACE,{"disambiguationData":[OSD([subQ6,subQ8,subQ9,subQ7,subQ4,subQ3,subQ2,subQ1,subQ0,subQ5,subQ10,subQ11])],"isStart":true})});}
            var sketch = newSketch(context, id + "F16", { "sketchPlane" : qUnion([Q0])});
            skLineSegment(sketch, "E79.0", {"start": v(-80, -80) * mm, "end": v(-80, 80) * mm});
            skArc(sketch, "E79.1", {"start": v(-70, 90) * mm, "mid": v(-77.07, 87.07) * mm, "end": v(-80, 80) * mm});
            skLineSegment(sketch, "E79.2", {"start": v(-70, 90) * mm, "end": v(70, 90) * mm});
            skArc(sketch, "E79.3", {"start": v(80, 80) * mm, "mid": v(77.07, 87.07) * mm, "end": v(70, 90) * mm});
            skLineSegment(sketch, "E79.4", {"start": v(80, -80) * mm, "end": v(80, 80) * mm});
            skArc(sketch, "E79.5", {"start": v(70, -90) * mm, "mid": v(77.07, -87.07) * mm, "end": v(80, -80) * mm});
            skLineSegment(sketch, "E79.6", {"start": v(-70, -90) * mm, "end": v(70, -90) * mm});
            skArc(sketch, "E79.7", {"start": v(-80, -80) * mm, "mid": v(-77.07, -87.07) * mm, "end": v(-70, -90) * mm});
            skCircle(sketch, "E79.8", {"center": v(-60, -67.5) * mm, "radius": 4 * mm});
            skCircle(sketch, "E79.9", {"center": v(-60, 67.5) * mm, "radius": 4 * mm});
            skCircle(sketch, "E79.10", {"center": v(60, 67.5) * mm, "radius": 4 * mm});
            skCircle(sketch, "E79.11", {"center": v(60, -67.5) * mm, "radius": 4 * mm});
            skLineSegment(sketch, "E79.12", {"start": v(60, 40.3) * mm, "end": v(60, -40.3) * mm});
            skArc(sketch, "E79.13", {"start": v(56.15, -48.18) * mm, "mid": v(58.99, -44.68) * mm, "end": v(60, -40.3) * mm});
            skArc(sketch, "E79.14", {"start": v(-56.15, -48.18) * mm, "mid": v(0, -67.5) * mm, "end": v(56.15, -48.18) * mm});
            skArc(sketch, "E79.15", {"start": v(-60, -40.3) * mm, "mid": v(-58.99, -44.68) * mm, "end": v(-56.15, -48.18) * mm});
            skLineSegment(sketch, "E79.16", {"start": v(-60, 40.3) * mm, "end": v(-60, -40.3) * mm});
            skArc(sketch, "E79.17", {"start": v(-56.15, 48.18) * mm, "mid": v(-58.99, 44.68) * mm, "end": v(-60, 40.3) * mm});
            skArc(sketch, "E79.18", {"start": v(56.15, 48.18) * mm, "mid": v(0, 67.5) * mm, "end": v(-56.15, 48.18) * mm});
            skArc(sketch, "E79.19", {"start": v(60, 40.3) * mm, "mid": v(58.99, 44.68) * mm, "end": v(56.15, 48.18) * mm});
            skCircle(sketch, "E80", {"center": v(0, 120) * mm, "radius": 6 * mm});
            skPoint(sketch, "E80.centerSnap0", {"position": v(0, 90) * mm});
            skLineSegment(sketch, "E81", {"start": v(-33, 90) * mm, "end": v(-15, 108) * mm});
            skLineSegment(sketch, "E82", {"start": v(-15, 108) * mm, "end": v(-15, 120) * mm});
            skLineSegment(sketch, "E83", {"start": v(33, 90) * mm, "end": v(15, 108) * mm});
            skLineSegment(sketch, "E84", {"start": v(15, 108) * mm, "end": v(15, 120) * mm});
            skArc(sketch, "E85", {"start": v(15, 120) * mm, "mid": v(0, 135) * mm, "end": v(-15, 120) * mm});
            skLineSegment(sketch, "E86", {"start": v(0, 90) * mm, "end": v(0, 120) * mm, "construction": true});
            skLineSegment(sketch, "E87", {"start": v(-80, 0) * mm, "end": v(80, 0) * mm, "construction": true});
            skArc(sketch, "E88.MirrorCS", {"start": v(-15, 120) * mm, "mid": v(0, 135) * mm, "end": v(15, 120) * mm});
            skLineSegment(sketch, "E89.MirrorCS", {"start": v(33, -90) * mm, "end": v(15, -108) * mm});
            skLineSegment(sketch, "E90.MirrorCS", {"start": v(15, -108) * mm, "end": v(15, -120) * mm});
            skArc(sketch, "E91.MirrorCS", {"start": v(15, -120) * mm, "mid": v(0, -135) * mm, "end": v(-15, -120) * mm});
            skLineSegment(sketch, "E92.MirrorCS", {"start": v(-15, -108) * mm, "end": v(-15, -120) * mm});
            skLineSegment(sketch, "E93.MirrorCS", {"start": v(-33, -90) * mm, "end": v(-15, -108) * mm});
            skLineSegment(sketch, "E94.MirrorCS", {"start": v(0, -90) * mm, "end": v(0, -120) * mm, "construction": true});
            skCircle(sketch, "E95.MirrorC", {"center": v(0, -120) * mm, "radius": 6 * mm});
            skSolve(sketch);
        }
        {
            var Q0;
            Q0=makeQuery(id+"F16.imprint","IMPRINT",FACE,{"disambiguationData":[TD([[makeQuery(id+"F16.imprint","IMPRINT",EDGE,{"derivedFrom":sQuery(id+"F16.wireOp",EDGE,"E79.0")}),-1.0]])]});
            var Q1;
            Q1=makeQuery(id+"F16.imprint","IMPRINT",FACE,{"disambiguationData":[TD([[makeQuery(id+"F16.imprint","IMPRINT",EDGE,{"derivedFrom":sQuery(id+"F16.wireOp",EDGE,"E80")}),1.0]])]});
            var Q2;
            {var subQ0=sQuery(id+"F16.wireOp",EDGE,"E89.MirrorCS");Q2=makeQuery(id+"F16.imprint","IMPRINT",FACE,{"disambiguationData":[TD([[makeQuery(id+"F16.imprint","IMPRINT",EDGE,{"derivedFrom":subQ0}),-1.0]])]});}
            var Q3;
            Q3=makeQuery(id+"F2.opExtrude","CAP_FACE",FACE,{"disambiguationData":[OSD([sQuery(id+"F0.wireOp",EDGE,"E12"),sQuery(id+"F0.wireOp",EDGE,"E13"),sQuery(id+"F0.wireOp",EDGE,"E14"),sQuery(id+"F0.wireOp",EDGE,"E15"),sQuery(id+"F0.wireOp",EDGE,"E17.filletArc"),sQuery(id+"F0.wireOp",EDGE,"E18.filletArc"),sQuery(id+"F0.wireOp",EDGE,"E19.filletArc"),sQuery(id+"F0.wireOp",EDGE,"E20.filletArc"),sQuery(id+"F0.wireOp",EDGE,"E25.0"),sQuery(id+"F0.wireOp",EDGE,"E25.1"),sQuery(id+"F0.wireOp",EDGE,"E25.2"),sQuery(id+"F0.wireOp",EDGE,"E25.3"),sQuery(id+"F0.wireOp",EDGE,"E25.4"),sQuery(id+"F0.wireOp",EDGE,"E25.5"),sQuery(id+"F0.wireOp",EDGE,"E25.6"),sQuery(id+"F0.wireOp",EDGE,"E25.7")])],"isStart":false});
            extrude(context, id + "F17", {"entities" : qUnion([Q0, Q1, Q2]), "endBound" : BoundingType.UP_TO_SURFACE, "endBoundEntityFace" : qUnion([Q3]), "depth" : 25 * mm});
        }
    });
